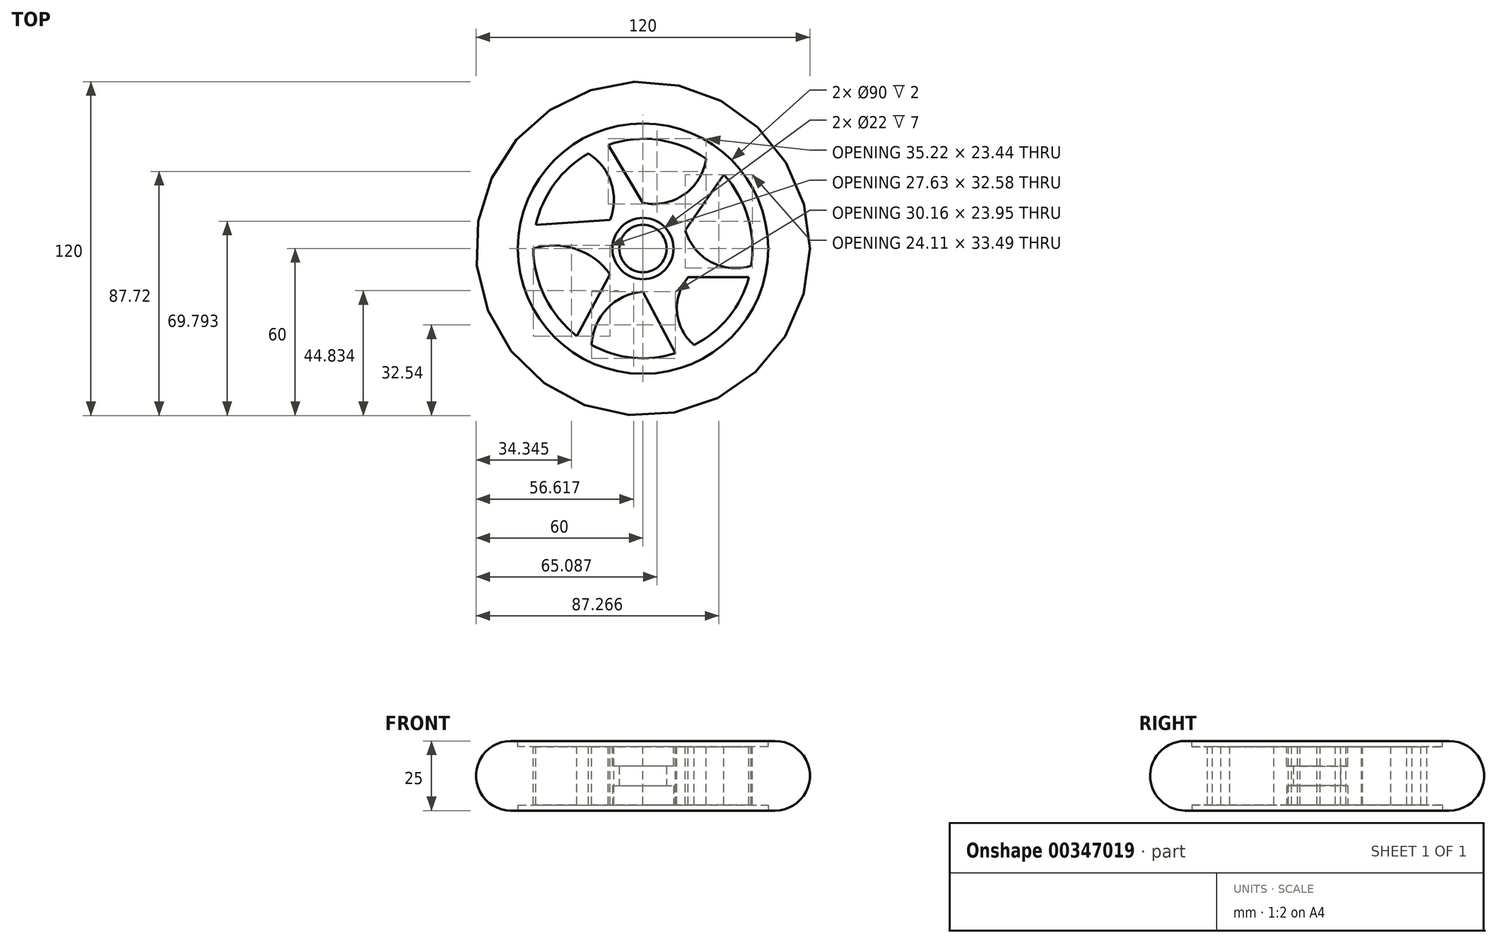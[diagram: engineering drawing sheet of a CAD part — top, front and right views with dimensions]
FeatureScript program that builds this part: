
annotation { "Feature Type Name" : "Feature", "Feature Type Description" : "" }
export const myFeature = defineFeature(function(context is Context, id is Id, definition is map)
    precondition{}
    {
        {
            var Q0;
            Q0=qCreatedBy(makeId("Top.planeOp"),FACE);
            var sketch = newSketch(context, id + "F0", { "sketchPlane" : qUnion([Q0])});
            skCircle(sketch, "E0", {"center": v(0, 0) * mm, "radius": 60 * mm});
            skSolve(sketch);
        }
        {
            var Q0;
            Q0=makeQuery(id+"F0.imprint","IMPRINT",FACE,{"disambiguationData":[TD([[makeQuery(id+"F0.imprint","IMPRINT",EDGE,{"derivedFrom":sQuery(id+"F0.wireOp",EDGE,"E0")}),1.0]])]});
            extrude(context, id + "F1", {"entities" : qUnion([Q0]), "depth" : 25 * mm});
        }
        {
            var Q0;
            Q0=makeQuery(id+"F1.opExtrude","CAP_FACE",FACE,{"disambiguationData":[OSD([sQuery(id+"F0.wireOp",EDGE,"E0")])],"isStart":false});
            var sketch = newSketch(context, id + "F2", { "sketchPlane" : qUnion([Q0])});
            skCircle(sketch, "E1", {"center": v(0, 0) * mm, "radius": 45 * mm});
            skSolve(sketch);
        }
        {
            var Q0;
            Q0=makeQuery(id+"F2.imprint","IMPRINT",FACE,{"disambiguationData":[TD([[makeQuery(id+"F2.imprint","IMPRINT",EDGE,{"derivedFrom":sQuery(id+"F2.wireOp",EDGE,"E1")}),1.0]])]});
            extrude(context, id + "F3", {"entities" : qUnion([Q0]), "operationType" : NewBodyOperationType.REMOVE, "oppositeDirection" : true, "depth" : 2 * mm});
        }
        {
            var Q0;
            Q0=makeQuery(id+"F3.boolean.opBoolean","COPY",FACE,{"derivedFrom":makeQuery(id+"F3.opExtrude","CAP_FACE",FACE,{"disambiguationData":[OSD([sQuery(id+"F2.wireOp",EDGE,"E1")])],"isStart":false})});
            var sketch = newSketch(context, id + "F4", { "sketchPlane" : qUnion([Q0])});
            skCircle(sketch, "E2", {"center": v(0, 0) * mm, "radius": 11 * mm});
            skSolve(sketch);
        }
        {
            var Q0;
            Q0=makeQuery(id+"F4.imprint","IMPRINT",FACE,{"disambiguationData":[TD([[makeQuery(id+"F4.imprint","IMPRINT",EDGE,{"derivedFrom":sQuery(id+"F4.wireOp",EDGE,"E2")}),1.0]])]});
            extrude(context, id + "F5", {"entities" : qUnion([Q0]), "operationType" : NewBodyOperationType.REMOVE, "oppositeDirection" : true, "depth" : 7 * mm});
        }
        {
            var Q0;
            Q0=makeQuery(id+"F1.opExtrude","CAP_FACE",FACE,{"disambiguationData":[OSD([sQuery(id+"F0.wireOp",EDGE,"E0")])],"isStart":true});
            var sketch = newSketch(context, id + "F6", { "sketchPlane" : qUnion([Q0])});
            skCircle(sketch, "E3", {"center": v(0, 0) * mm, "radius": 45 * mm});
            skSolve(sketch);
        }
        {
            var Q0;
            Q0=makeQuery(id+"F6.imprint","IMPRINT",FACE,{"disambiguationData":[TD([[makeQuery(id+"F6.imprint","IMPRINT",EDGE,{"derivedFrom":sQuery(id+"F6.wireOp",EDGE,"E3")}),1.0]])]});
            extrude(context, id + "F7", {"entities" : qUnion([Q0]), "operationType" : NewBodyOperationType.REMOVE, "oppositeDirection" : true, "depth" : 2 * mm});
        }
        {
            var Q0;
            Q0=makeQuery(id+"F7.boolean.opBoolean","COPY",FACE,{"derivedFrom":makeQuery(id+"F7.opExtrude","CAP_FACE",FACE,{"disambiguationData":[OSD([sQuery(id+"F6.wireOp",EDGE,"E3")])],"isStart":false})});
            var sketch = newSketch(context, id + "F8", { "sketchPlane" : qUnion([Q0])});
            skCircle(sketch, "E4", {"center": v(0, 0) * mm, "radius": 11 * mm});
            skSolve(sketch);
        }
        {
            var Q0;
            Q0=makeQuery(id+"F8.imprint","IMPRINT",FACE,{"disambiguationData":[TD([[makeQuery(id+"F8.imprint","IMPRINT",EDGE,{"derivedFrom":sQuery(id+"F8.wireOp",EDGE,"E4")}),1.0]])]});
            extrude(context, id + "F9", {"entities" : qUnion([Q0]), "operationType" : NewBodyOperationType.REMOVE, "oppositeDirection" : true, "depth" : 7 * mm});
        }
        {
            var Q0;
            Q0=makeQuery(id+"F9.boolean.opBoolean","COPY",FACE,{"derivedFrom":makeQuery(id+"F9.opExtrude","CAP_FACE",FACE,{"disambiguationData":[OSD([sQuery(id+"F8.wireOp",EDGE,"E4")])],"isStart":false})});
            var sketch = newSketch(context, id + "F10", { "sketchPlane" : qUnion([Q0])});
            skCircle(sketch, "E5", {"center": v(0, 0) * mm, "radius": 8.5 * mm});
            skSolve(sketch);
        }
        {
            var Q0;
            Q0=makeQuery(id+"F10.imprint","IMPRINT",FACE,{"disambiguationData":[TD([[makeQuery(id+"F10.imprint","IMPRINT",EDGE,{"derivedFrom":sQuery(id+"F10.wireOp",EDGE,"E5")}),1.0]])]});
            extrude(context, id + "F11", {"entities" : qUnion([Q0]), "operationType" : NewBodyOperationType.REMOVE, "oppositeDirection" : true, "depth" : 25 * mm});
        }
        {
            var Q0;
            Q0=makeQuery(id+"F1.opExtrude","CAP_EDGE",EDGE,{"disambiguationData":[OSD([sQuery(id+"F0.wireOp",EDGE,"E0")])],"isStart":false});
            var Q1;
            Q1=makeQuery(id+"F1.opExtrude","CAP_EDGE",EDGE,{"disambiguationData":[OSD([sQuery(id+"F0.wireOp",EDGE,"E0")])],"isStart":true});
            fillet(context, id + "F12", {"entities" : qUnion([Q0, Q1]), "radius" : 12.5 * mm, "tangentPropagation" : true, "allowEdgeOverflow" : false});
        }
        {
            var Q0;
            Q0=makeQuery(id+"F3.boolean.opBoolean","COPY",FACE,{"derivedFrom":makeQuery(id+"F3.opExtrude","CAP_FACE",FACE,{"disambiguationData":[OSD([sQuery(id+"F2.wireOp",EDGE,"E1")])],"isStart":false})});
            var sketch = newSketch(context, id + "F13", { "sketchPlane" : qUnion([Q0])});
            skCircle(sketch, "E6", {"center": v(0, 0) * mm, "radius": 39.45 * mm});
            skSolve(sketch);
        }
        {
            var Q0;
            Q0=makeQuery(id+"F13.imprint","IMPRINT",FACE,{"disambiguationData":[TD([[makeQuery(id+"F13.imprint","IMPRINT",EDGE,{"derivedFrom":sQuery(id+"F13.wireOp",EDGE,"E6")}),1.0]])]});
            var sketch = newSketch(context, id + "F14", { "sketchPlane" : qUnion([Q0])});
            skSolve(sketch);
        }
        {
            var Q0;
            Q0=makeQuery(id+"F14.imprint","IMPRINT",FACE,{"disambiguationData":[TD([[makeQuery(id+"F14.imprint","IMPRINT",EDGE,{"derivedFrom":makeQuery(id+"F13.imprint","IMPRINT",EDGE,{"derivedFrom":sQuery(id+"F13.wireOp",EDGE,"E6")})}),1.0]])]});
            var sketch = newSketch(context, id + "F15", { "sketchPlane" : qUnion([Q0])});
            skArc(sketch, "E7", {"start": v(-11.84, -9.2) * mm, "mid": v(-24.17, -0.15) * mm, "end": v(-39.47, 0) * mm});
            skLineSegment(sketch, "E8", {"start": v(-11.84, -9.2) * mm, "end": v(-23.73, -31.46) * mm});
            skArc(sketch, "E9", {"start": v(-39.47, 0) * mm, "mid": v(-35.17, -17.51) * mm, "end": v(-23.73, -31.46) * mm});
            skArc(sketch, "E10", {"start": v(0, -15.48) * mm, "mid": v(-12.88, -21.55) * mm, "end": v(-18.46, -34.65) * mm});
            skLineSegment(sketch, "E11", {"start": v(0, -15.48) * mm, "end": v(11.7, -37.6) * mm});
            skArc(sketch, "E12", {"start": v(-18.46, -34.65) * mm, "mid": v(-3.69, -39.26) * mm, "end": v(11.7, -37.6) * mm});
            skArc(sketch, "E13", {"start": v(16.27, -10.32) * mm, "mid": v(12.24, -22.93) * mm, "end": v(18.4, -34.65) * mm});
            skLineSegment(sketch, "E14", {"start": v(16.27, -10.32) * mm, "end": v(38.07, -10.32) * mm});
            skArc(sketch, "E15", {"start": v(15.2, 6.56) * mm, "mid": v(24.36, -4.78) * mm, "end": v(38.87, -6.2) * mm});
            skLineSegment(sketch, "E16", {"start": v(15.2, 6.56) * mm, "end": v(29.1, 26.54) * mm});
            skArc(sketch, "E17", {"start": v(0, 16.39) * mm, "mid": v(14.75, 19.42) * mm, "end": v(22.7, 32.2) * mm});
            skLineSegment(sketch, "E18", {"start": v(0, 16.39) * mm, "end": v(-12.52, 37.25) * mm});
            skArc(sketch, "E19", {"start": v(22.7, 32.2) * mm, "mid": v(5.7, 39.06) * mm, "end": v(-12.52, 37.25) * mm});
            skArc(sketch, "E20", {"start": v(38.87, -6.2) * mm, "mid": v(37.73, 11.29) * mm, "end": v(29.1, 26.54) * mm});
            skArc(sketch, "E21", {"start": v(18.4, -34.65) * mm, "mid": v(30.85, -24.6) * mm, "end": v(38.07, -10.32) * mm});
            skArc(sketch, "E22", {"start": v(-11.86, 10.34) * mm, "mid": v(-11.4, 23.66) * mm, "end": v(-19.61, 34.17) * mm});
            skLineSegment(sketch, "E23", {"start": v(-11.86, 10.34) * mm, "end": v(-38.48, 8.5) * mm});
            skArc(sketch, "E24", {"start": v(-19.61, 34.17) * mm, "mid": v(-31.77, 23.34) * mm, "end": v(-38.48, 8.5) * mm});
            skSolve(sketch);
        }
        {
            var Q0;
            Q0 = qSketchRegion(id + "F15", true);
            extrude(context, id + "F16", {"entities" : qUnion([Q0]), "operationType" : NewBodyOperationType.REMOVE, "oppositeDirection" : true, "depth" : 25 * mm, "offsetDistance" : 25 * mm});
        }
    });
